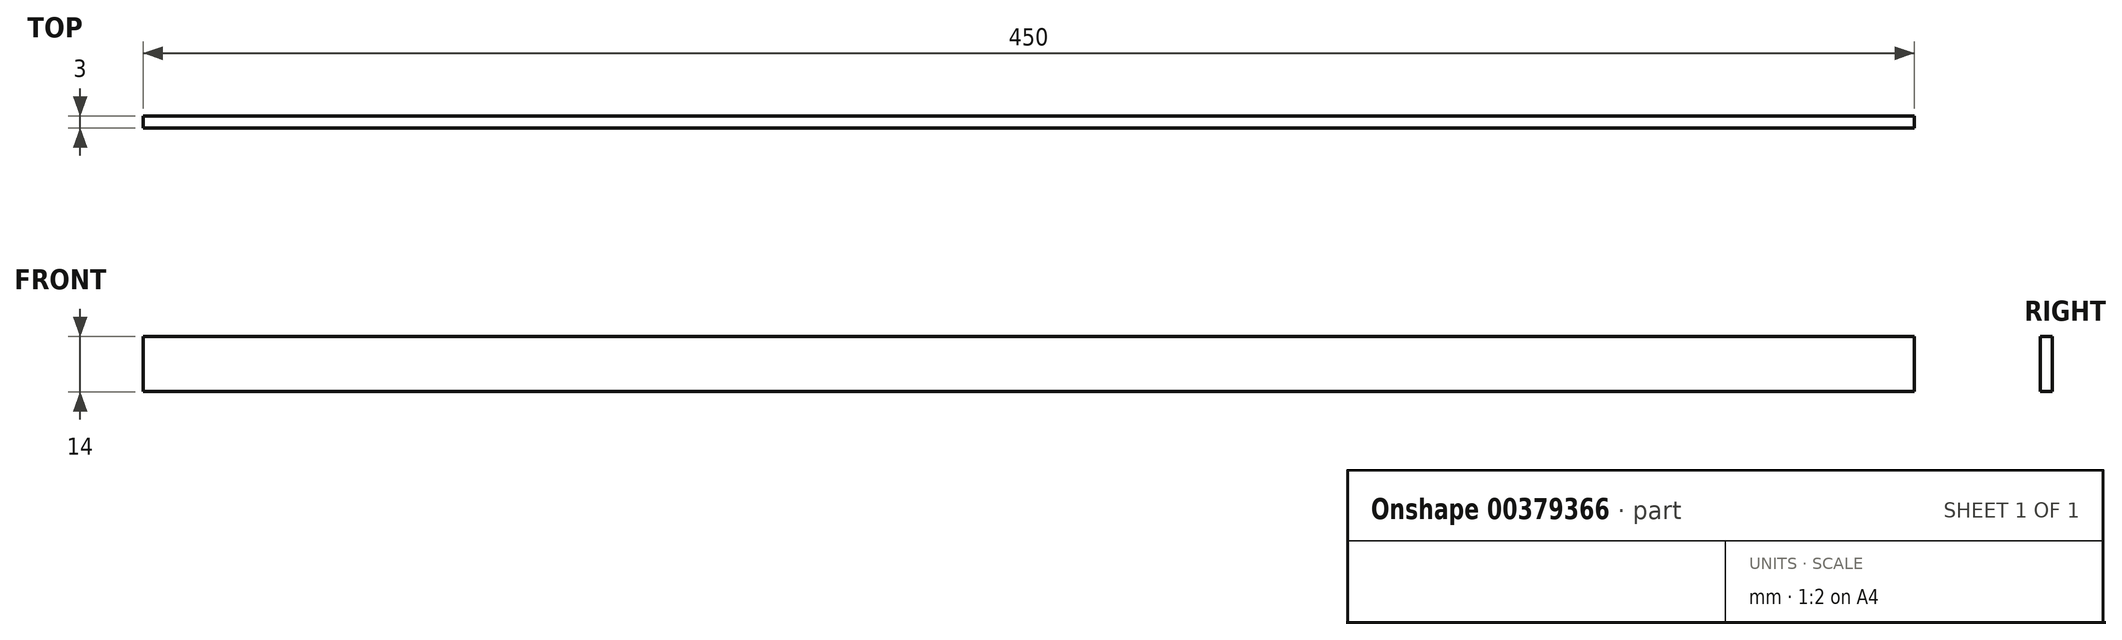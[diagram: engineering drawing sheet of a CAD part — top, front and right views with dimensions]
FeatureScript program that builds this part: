
annotation { "Feature Type Name" : "Feature", "Feature Type Description" : "" }
export const myFeature = defineFeature(function(context is Context, id is Id, definition is map)
    precondition{}
    {
        {
            var Q0;
            Q0=qCreatedBy(makeId("Front.planeOp"),FACE);
            var sketch = newSketch(context, id + "F0", { "sketchPlane" : qUnion([Q0])});
            skLineSegment(sketch, "E0.bottom", {"start": v(-5.81, 35.27) * mm, "end": v(444.19, 35.27) * mm});
            skLineSegment(sketch, "E0.top", {"start": v(-5.81, 21.27) * mm, "end": v(444.19, 21.27) * mm});
            skLineSegment(sketch, "E0.left", {"start": v(-5.81, 35.27) * mm, "end": v(-5.81, 21.27) * mm});
            skLineSegment(sketch, "E0.right", {"start": v(444.19, 35.27) * mm, "end": v(444.19, 21.27) * mm});
            skLineSegment(sketch, "E1", {"start": v(69.19, 35.27) * mm, "end": v(69.19, 21.27) * mm});
            skLineSegment(sketch, "E2", {"start": v(369.19, 35.27) * mm, "end": v(369.19, 21.27) * mm});
            skLineSegment(sketch, "E3", {"start": v(144.19, 35.27) * mm, "end": v(144.19, 21.27) * mm});
            skLineSegment(sketch, "E4", {"start": v(294.19, 35.27) * mm, "end": v(294.19, 21.27) * mm});
            skSolve(sketch);
        }
        {
            var Q0;
            Q0 = qSketchRegion(id + "F0", true);
            extrude(context, id + "F1", {"entities" : qUnion([Q0]), "depth" : 3 * mm, "offsetDistance" : 25 * mm});
        }
    });
